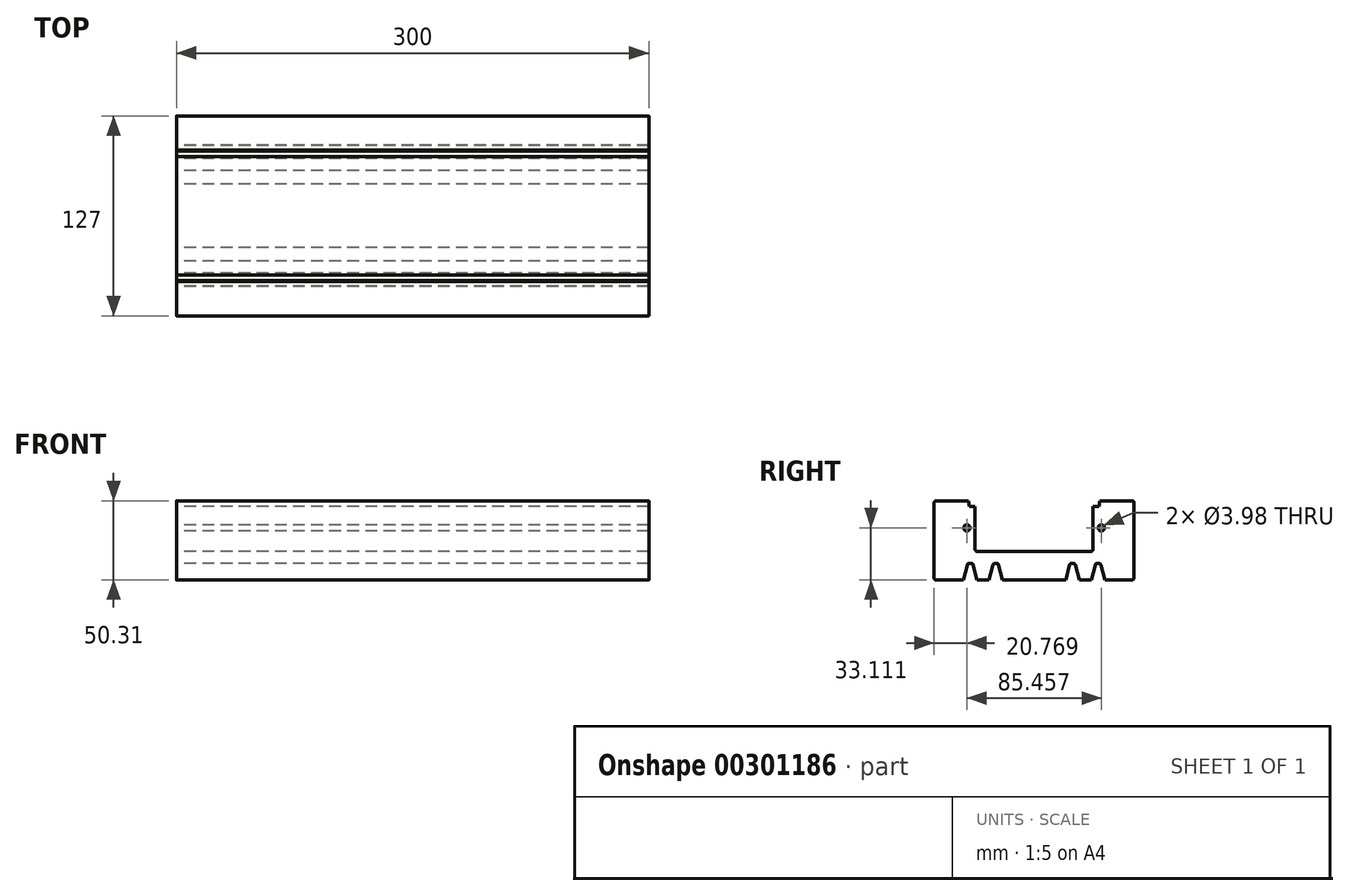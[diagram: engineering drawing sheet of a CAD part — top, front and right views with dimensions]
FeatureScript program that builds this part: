
annotation { "Feature Type Name" : "Feature", "Feature Type Description" : "" }
export const myFeature = defineFeature(function(context is Context, id is Id, definition is map)
    precondition{}
    {
        {
            var Q0;
            Q0=qCreatedBy(makeId("Right.planeOp"),FACE);
            var sketch = newSketch(context, id + "F0", { "sketchPlane" : qUnion([Q0])});
            skLineSegment(sketch, "E0.bottom", {"start": v(-60.1, 28.68) * mm, "end": v(-39.64, 28.68) * mm});
            skLineSegment(sketch, "E0.top", {"start": v(-60.1, -21.63) * mm, "end": v(-42.76, -21.63) * mm});
            skLineSegment(sketch, "E0.left", {"start": v(-61.37, 27.4) * mm, "end": v(-61.37, 25.52) * mm});
            skLineSegment(sketch, "E0.right", {"start": v(65.63, 27.4) * mm, "end": v(65.63, 25.52) * mm});
            skPoint(sketch, "E0.middle", {"position": v(2.13, 3.53) * mm});
            skLineSegment(sketch, "E1.direction1", {"start": v(-61.37, 25.52) * mm, "end": v(-48.67, 25.52) * mm, "construction": true});
            skLineSegment(sketch, "E1.direction2", {"start": v(-61.37, 15.41) * mm, "end": v(-61.37, 9) * mm, "construction": true});
            skLineSegment(sketch, "E2.trimOffspring", {"start": v(-61.37, -1.1) * mm, "end": v(-61.37, -7.5) * mm});
            skLineSegment(sketch, "E3.trimOffspring", {"start": v(-61.37, 15.41) * mm, "end": v(-61.37, 9) * mm});
            skLineSegment(sketch, "E4.trimOffspring", {"start": v(-61.37, -17.6) * mm, "end": v(-61.37, -20.36) * mm});
            skPoint(sketch, "E5.visualSharp", {"position": v(-61.37, 28.68) * mm});
            skArc(sketch, "E5.filletArc", {"start": v(-60.1, 28.68) * mm, "mid": v(-61, 28.3) * mm, "end": v(-61.37, 27.4) * mm});
            skPoint(sketch, "E6.visualSharp", {"position": v(-61.37, -21.63) * mm});
            skArc(sketch, "E6.filletArc", {"start": v(-61.37, -20.36) * mm, "mid": v(-61, -21.26) * mm, "end": v(-60.1, -21.63) * mm});
            skLineSegment(sketch, "E7", {"start": v(2.13, 3.53) * mm, "end": v(2.13, 45.9) * mm, "construction": true});
            skLineSegment(sketch, "E8.trimOffspring", {"start": v(65.63, 15.41) * mm, "end": v(65.63, 9) * mm});
            skLineSegment(sketch, "E9.trimOffspring", {"start": v(65.63, -1.1) * mm, "end": v(65.63, -7.5) * mm});
            skLineSegment(sketch, "E10.trimOffspring", {"start": v(65.63, -17.6) * mm, "end": v(65.63, -20.36) * mm});
            skLineSegment(sketch, "E11", {"start": v(-42.76, -21.63) * mm, "end": v(-40.31, -12.02) * mm});
            skLineSegment(sketch, "E12", {"start": v(-39.08, -11.07) * mm, "end": v(-37.75, -11.07) * mm});
            skLineSegment(sketch, "E13.MirrorCS", {"start": v(-34.23, -21.63) * mm, "end": v(-36.71, -11.87) * mm});
            skPoint(sketch, "E14.start.orphan", {"position": v(-38.5, -11.07) * mm});
            skLineSegment(sketch, "E15.1.0.0", {"start": v(-17.98, -21.63) * mm, "end": v(-20.42, -12.02) * mm});
            skLineSegment(sketch, "E15.1.0.1", {"start": v(-26.5, -21.63) * mm, "end": v(-24.06, -12.02) * mm});
            skLineSegment(sketch, "E15.1.0.2", {"start": v(-22.82, -11.07) * mm, "end": v(-21.65, -11.07) * mm});
            skLineSegment(sketch, "E15.4.0.0", {"start": v(30.8, -21.63) * mm, "end": v(28.35, -12.02) * mm});
            skLineSegment(sketch, "E15.4.0.1", {"start": v(22.27, -21.63) * mm, "end": v(24.71, -12.02) * mm});
            skLineSegment(sketch, "E15.4.0.2", {"start": v(25.94, -11.07) * mm, "end": v(27.12, -11.07) * mm});
            skLineSegment(sketch, "E15.5.0.0", {"start": v(47.05, -21.63) * mm, "end": v(44.6, -12.02) * mm});
            skLineSegment(sketch, "E15.5.0.1", {"start": v(38.52, -21.63) * mm, "end": v(40.97, -12.02) * mm});
            skLineSegment(sketch, "E15.5.0.2", {"start": v(42.2, -11.07) * mm, "end": v(43.37, -11.07) * mm});
            skLineSegment(sketch, "E15.direction1", {"start": v(-34.23, -21.63) * mm, "end": v(-26.5, -21.63) * mm, "construction": true});
            skLineSegment(sketch, "E16.trimOffspring", {"start": v(-34.23, -21.63) * mm, "end": v(-26.5, -21.63) * mm});
            skLineSegment(sketch, "E17.trimOffspring", {"start": v(-17.98, -21.63) * mm, "end": v(22.27, -21.63) * mm});
            skLineSegment(sketch, "E18.trimOffspring", {"start": v(47.05, -21.63) * mm, "end": v(64.36, -21.63) * mm});
            skLineSegment(sketch, "E19.trimOffspring", {"start": v(30.8, -21.63) * mm, "end": v(38.52, -21.63) * mm});
            skPoint(sketch, "E20.visualSharp", {"position": v(65.63, 28.68) * mm});
            skArc(sketch, "E20.filletArc", {"start": v(65.63, 27.4) * mm, "mid": v(65.26, 28.3) * mm, "end": v(64.36, 28.68) * mm});
            skPoint(sketch, "E21.visualSharp", {"position": v(65.63, -21.63) * mm});
            skArc(sketch, "E21.filletArc", {"start": v(64.36, -21.63) * mm, "mid": v(65.26, -21.26) * mm, "end": v(65.63, -20.36) * mm});
            skLineSegment(sketch, "E22", {"start": v(-39.64, 28.68) * mm, "end": v(-39.03, 25.22) * mm});
            skLineSegment(sketch, "E23", {"start": v(-39.03, 25.22) * mm, "end": v(-35.36, 25.22) * mm});
            skLineSegment(sketch, "E24", {"start": v(-35.36, 25.22) * mm, "end": v(-35.36, -2.2) * mm});
            skLineSegment(sketch, "E25", {"start": v(-34.1, -3.47) * mm, "end": v(2.13, -3.47) * mm});
            skLineSegment(sketch, "E26.trimOffspring", {"start": v(43.9, 28.68) * mm, "end": v(64.36, 28.68) * mm});
            skLineSegment(sketch, "E27.MirrorCS", {"start": v(38.35, -3.47) * mm, "end": v(2.13, -3.47) * mm});
            skLineSegment(sketch, "E28.MirrorCS", {"start": v(39.62, 25.22) * mm, "end": v(39.62, -2.2) * mm});
            skLineSegment(sketch, "E29.MirrorCS", {"start": v(43.28, 25.22) * mm, "end": v(39.62, 25.22) * mm});
            skLineSegment(sketch, "E30.MirrorCS", {"start": v(43.9, 28.68) * mm, "end": v(43.28, 25.22) * mm});
            skPoint(sketch, "E31.visualSharp", {"position": v(-35.36, -3.47) * mm});
            skArc(sketch, "E31.filletArc", {"start": v(-35.36, -2.2) * mm, "mid": v(-35, -3.1) * mm, "end": v(-34.1, -3.47) * mm});
            skPoint(sketch, "E32.visualSharp", {"position": v(39.62, -3.47) * mm});
            skArc(sketch, "E32.filletArc", {"start": v(38.35, -3.47) * mm, "mid": v(39.25, -3.1) * mm, "end": v(39.62, -2.2) * mm});
            skPoint(sketch, "E33.visualSharp", {"position": v(-40.07, -11.07) * mm});
            skArc(sketch, "E33.filletArc", {"start": v(-39.08, -11.07) * mm, "mid": v(-39.86, -11.33) * mm, "end": v(-40.31, -12.02) * mm});
            skPoint(sketch, "E34.visualSharp", {"position": v(-23.81, -11.07) * mm});
            skArc(sketch, "E34.filletArc", {"start": v(-22.82, -11.07) * mm, "mid": v(-23.6, -11.33) * mm, "end": v(-24.06, -12.02) * mm});
            skPoint(sketch, "E35.visualSharp", {"position": v(-20.66, -11.07) * mm});
            skArc(sketch, "E35.filletArc", {"start": v(-20.42, -12.02) * mm, "mid": v(-20.87, -11.33) * mm, "end": v(-21.65, -11.07) * mm});
            skPoint(sketch, "E36.visualSharp", {"position": v(-36.92, -11.07) * mm});
            skArc(sketch, "E36.filletArc", {"start": v(-36.71, -11.87) * mm, "mid": v(-37.1, -11.3) * mm, "end": v(-37.75, -11.07) * mm});
            skPoint(sketch, "E37.visualSharp", {"position": v(24.96, -11.07) * mm});
            skArc(sketch, "E37.filletArc", {"start": v(25.94, -11.07) * mm, "mid": v(25.16, -11.33) * mm, "end": v(24.71, -12.02) * mm});
            skPoint(sketch, "E38.visualSharp", {"position": v(28.1, -11.07) * mm});
            skArc(sketch, "E38.filletArc", {"start": v(28.35, -12.02) * mm, "mid": v(27.9, -11.33) * mm, "end": v(27.12, -11.07) * mm});
            skPoint(sketch, "E39.visualSharp", {"position": v(41.21, -11.07) * mm});
            skArc(sketch, "E39.filletArc", {"start": v(42.2, -11.07) * mm, "mid": v(41.42, -11.33) * mm, "end": v(40.97, -12.02) * mm});
            skPoint(sketch, "E40.visualSharp", {"position": v(44.36, -11.07) * mm});
            skArc(sketch, "E40.filletArc", {"start": v(44.6, -12.02) * mm, "mid": v(44.15, -11.33) * mm, "end": v(43.37, -11.07) * mm});
            skCircle(sketch, "E41", {"center": v(-40.6, 11.48) * mm, "radius": 1.99 * mm});
            skCircle(sketch, "E42.MirrorC", {"center": v(44.86, 11.48) * mm, "radius": 1.99 * mm});
            skLineSegment(sketch, "E43", {"start": v(-61.37, 25.52) * mm, "end": v(-61.37, -17.6) * mm});
            skLineSegment(sketch, "E44", {"start": v(65.63, 25.52) * mm, "end": v(65.63, -17.6) * mm});
            skSolve(sketch);
        }
        {
            var Q0;
            Q0 = qSketchRegion(id + "F0", true);
            extrude(context, id + "F1", {"entities" : qUnion([Q0]), "endBound" : BoundingType.SYMMETRIC, "depth" : 300 * mm});
        }
    });
